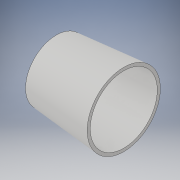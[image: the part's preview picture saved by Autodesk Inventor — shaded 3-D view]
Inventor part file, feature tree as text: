
AUTODESK INVENTOR PART (.ipt)
format: ipt  version: 2019 (Build 230136000, 136)  size: 114,176 bytes
history: native  units: mm
features: revolve x1, sketch x1
ambient origin geometry x8: Origin, YZ Plane, XZ Plane, XY Plane, X Axis, Y Axis, Z Axis, Center Point
bodies: Solid1 (feature_tree)
feature tree (2):
  revolve  "Revolution1"  [1 undecoded]
  sketch  "Sketch1"  dims[d0=20.0mm d1=0.872665mm d2=9.0mm d3=22.0mm d4=90.0deg]
note: 1 required parameter value undecoded (feature->parameter linkage not recoverable at this tier; creation-order binding heuristic only, values carry confidence <= 0.55)
